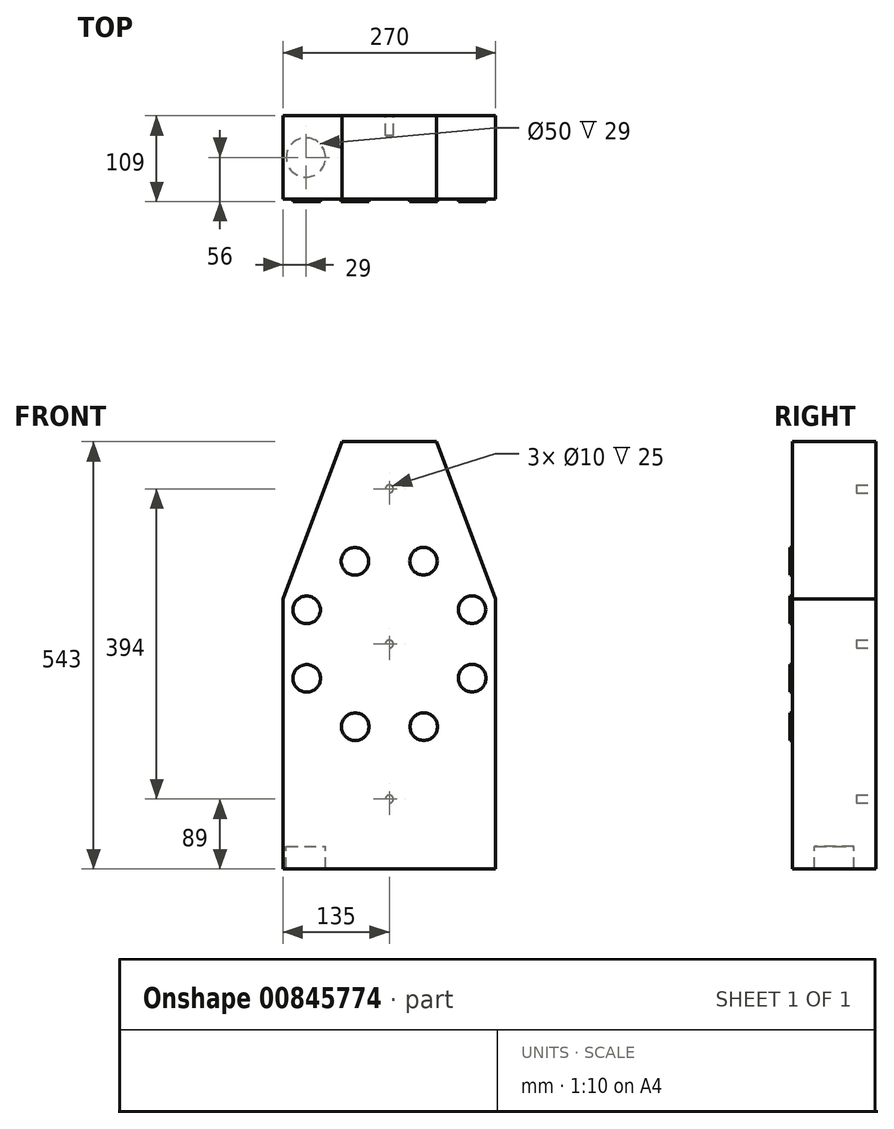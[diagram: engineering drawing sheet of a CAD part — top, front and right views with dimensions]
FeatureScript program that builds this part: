
annotation { "Feature Type Name" : "Feature", "Feature Type Description" : "" }
export const myFeature = defineFeature(function(context is Context, id is Id, definition is map)
    precondition{}
    {
        {
            var Q0;
            Q0=qCreatedBy(makeId("Front.planeOp"),FACE);
            var sketch = newSketch(context, id + "F0", { "sketchPlane" : qUnion([Q0])});
            skLineSegment(sketch, "E0.bottom", {"start": v(60, 257) * mm, "end": v(-60, 257) * mm});
            skLineSegment(sketch, "E0.top", {"start": v(135, -257) * mm, "end": v(-135, -257) * mm});
            skLineSegment(sketch, "E0.left", {"start": v(135, 57) * mm, "end": v(135, -257) * mm});
            skLineSegment(sketch, "E0.right", {"start": v(-135, 57) * mm, "end": v(-135, -257) * mm});
            skPoint(sketch, "E0.middle", {"position": v(0, 0) * mm});
            skLineSegment(sketch, "E1.bottom", {"start": v(-60, 257) * mm, "end": v(60, 257) * mm});
            skLineSegment(sketch, "E2", {"start": v(135, 57) * mm, "end": v(60, 257) * mm});
            skLineSegment(sketch, "E3", {"start": v(-60, 257) * mm, "end": v(-135, 57) * mm});
            skPoint(sketch, "E4.end.orphan", {"position": v(-60, 57) * mm});
            skPoint(sketch, "E5.orphan", {"position": v(-135, 257) * mm});
            skPoint(sketch, "E6.orphan", {"position": v(135, 257) * mm});
            skSolve(sketch);
        }
        {
            var Q0;
            Q0=makeQuery(id+"F0.imprint","IMPRINT",FACE,{"disambiguationData":[TD([[makeQuery(id+"F0.imprint","IMPRINT",EDGE,{"derivedFrom":sQuery(id+"F0.wireOp",EDGE,"E0.top")}),-1.0]])]});
            extrude(context, id + "F1", {"entities" : qUnion([Q0]), "endBound" : BoundingType.SYMMETRIC, "oppositeDirection" : true, "depth" : 106 * mm, "offsetDistance" : 25 * mm});
        }
        {
            var Q0;
            Q0=makeQuery(id+"F1.opExtrude","CAP_FACE",FACE,{"disambiguationData":[OSD([sQuery(id+"F0.wireOp",EDGE,"E0.top"),sQuery(id+"F0.wireOp",EDGE,"E0.left"),sQuery(id+"F0.wireOp",EDGE,"E0.right"),sQuery(id+"F0.wireOp",EDGE,"E1.bottom"),sQuery(id+"F0.wireOp",EDGE,"E2"),sQuery(id+"F0.wireOp",EDGE,"E3")])],"isStart":true});
            var sketch = newSketch(context, id + "F2", { "sketchPlane" : qUnion([Q0])});
            skCircle(sketch, "E7", {"center": v(105, 43.7) * mm, "radius": 17.5 * mm});
            skPoint(sketch, "E8.center", {"position": v(0, 0) * mm});
            skCircle(sketch, "E9.1.0", {"center": v(43.35, 105.15) * mm, "radius": 17.5 * mm});
            skCircle(sketch, "E9.2.0", {"center": v(-43.7, 105) * mm, "radius": 17.5 * mm});
            skCircle(sketch, "E9.3.0", {"center": v(-105.15, 43.35) * mm, "radius": 17.5 * mm});
            skCircle(sketch, "E9.4.0", {"center": v(-105, -43.7) * mm, "radius": 17.5 * mm});
            skCircle(sketch, "E9.5.0", {"center": v(-43.35, -105.15) * mm, "radius": 17.5 * mm});
            skCircle(sketch, "E9.6.0", {"center": v(43.7, -105) * mm, "radius": 17.5 * mm});
            skCircle(sketch, "E9.7.0", {"center": v(105.15, -43.35) * mm, "radius": 17.5 * mm});
            skSolve(sketch);
        }
        {
            var Q0;
            Q0 = qSketchRegion(id + "F2", true);
            extrude(context, id + "F3", {"entities" : qUnion([Q0]), "operationType" : NewBodyOperationType.ADD, "depth" : 3 * mm, "offsetDistance" : 25 * mm});
        }
        {
            var Q0;
            Q0=makeQuery(id+"F1.opExtrude","CAP_FACE",FACE,{"disambiguationData":[OSD([sQuery(id+"F0.wireOp",EDGE,"E0.top"),sQuery(id+"F0.wireOp",EDGE,"E0.left"),sQuery(id+"F0.wireOp",EDGE,"E0.right"),sQuery(id+"F0.wireOp",EDGE,"E1.bottom"),sQuery(id+"F0.wireOp",EDGE,"E2"),sQuery(id+"F0.wireOp",EDGE,"E3")])],"isStart":false});
            var sketch = newSketch(context, id + "F4", { "sketchPlane" : qUnion([Q0])});
            skCircle(sketch, "E10", {"center": v(0, 0) * mm, "radius": 5 * mm});
            skCircle(sketch, "E11", {"center": v(0, 197) * mm, "radius": 5 * mm});
            skCircle(sketch, "E12", {"center": v(0, -197) * mm, "radius": 5 * mm});
            skSolve(sketch);
        }
        {
            var Q0;
            Q0 = qSketchRegion(id + "F4", true);
            extrude(context, id + "F5", {"entities" : qUnion([Q0]), "operationType" : NewBodyOperationType.REMOVE, "oppositeDirection" : true, "depth" : 25 * mm, "offsetDistance" : 25 * mm});
        }
        {
            var Q0;
            Q0=makeQuery(id+"F1.opExtrude","SWEPT_FACE",FACE,{"disambiguationData":[OSD([sQuery(id+"F0.wireOp",EDGE,"E0.top")])]});
            var sketch = newSketch(context, id + "F6", { "sketchPlane" : qUnion([Q0])});
            skCircle(sketch, "E13", {"center": v(106, 0) * mm, "radius": 25 * mm});
            skCircle(sketch, "E14.MirrorC", {"center": v(-106, 0) * mm, "radius": 25 * mm});
            skSolve(sketch);
        }
        {
            var Q0;
            Q0=makeQuery(id+"F6.imprint","IMPRINT",FACE,{"disambiguationData":[TD([[makeQuery(id+"F6.imprint","IMPRINT",EDGE,{"derivedFrom":sQuery(id+"F6.wireOp",EDGE,"E13")}),1.0]])]});
            var Q1;
            Q1=makeQuery(id+"F6.imprint","IMPRINT",FACE,{"disambiguationData":[TD([[makeQuery(id+"F6.imprint","IMPRINT",EDGE,{"derivedFrom":sQuery(id+"F6.wireOp",EDGE,"E14.MirrorC")}),-1.0]])]});
            extrude(context, id + "F7", {"entities" : qUnion([Q0, Q1]), "operationType" : NewBodyOperationType.ADD, "depth" : 29 * mm, "offsetDistance" : 25 * mm});
        }
    });
